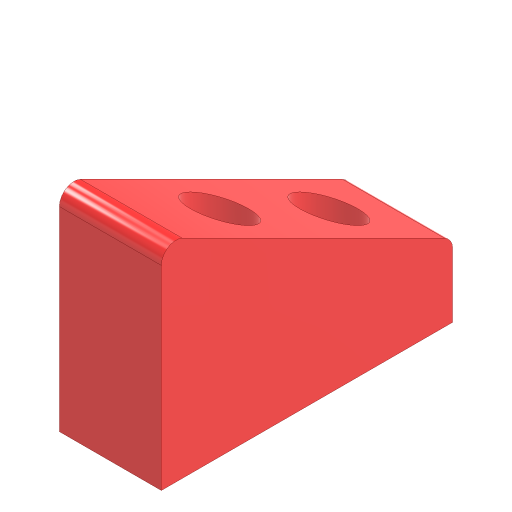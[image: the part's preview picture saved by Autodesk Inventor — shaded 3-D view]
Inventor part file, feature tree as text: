
AUTODESK INVENTOR PART (.ipt)
format: ipt  version: 2024.3 (Build 283343000, 343)  size: 308,224 bytes
history: native  units: mm
features: projected_geometry x5, sketch x4, extrude x3, fillet x1, plane x1, hole x1
ambient origin geometry x8: Origin, YZ Plane, XZ Plane, XY Plane, X Axis, Y Axis, Z Axis, Center Point
bodies: Solid1 (feature_tree)
feature tree (15):
  extrude  "Extrusion1"  Depth=40.0mm
  extrude  "Extrusion2"  Depth=10.0mm
  fillet  "Fillet1"  [1 undecoded]
  plane  "Work Plane1"
  hole  "Hole1"  [1 undecoded]
  extrude  "Extrusion3"  Depth=10.0mm
  sketch  "Sketch1"  dims[d0=30.0mm d1=40.0mm]
  sketch  "Sketch2"  dims[d2=14.0mm d3=0.0mm d4=10.0mm d5=0.0mm d6=0.0mm]
  projected_geometry  "Projected Loop1"
  sketch  "Sketch3"  dims[d7=2.0mm d8=-11.0mm]
  projected_geometry  "Projected Loop2"
  projected_geometry  "Projected Loop3"
  sketch  "Sketch4"  dims[d9=15.0mm d10=10.0mm d11=4.5mm d12=6.0mm d13=8.0mm d14=4.6mm d15=90.0deg d16=8.0mm d17=20.594885mm d18=0.0mm d19=0.0mm]
  projected_geometry  "Projected Loop4"
  projected_geometry  "Projected Loop5"
note: 2 required parameter values undecoded (feature->parameter linkage not recoverable at this tier; creation-order binding heuristic only, values carry confidence <= 0.55)
